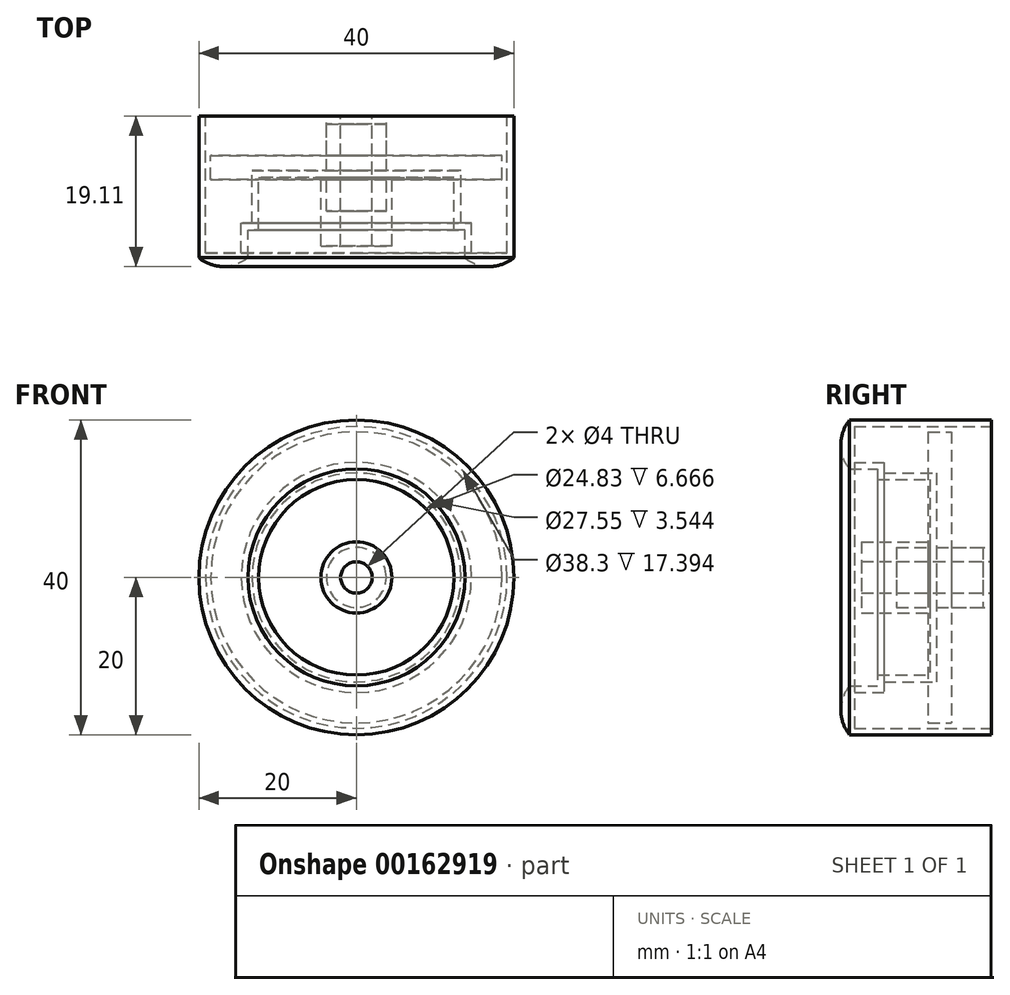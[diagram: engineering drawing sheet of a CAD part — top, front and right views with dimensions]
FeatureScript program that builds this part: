
annotation { "Feature Type Name" : "Feature", "Feature Type Description" : "" }
export const myFeature = defineFeature(function(context is Context, id is Id, definition is map)
    precondition{}
    {
        {
            var Q0;
            Q0=qCreatedBy(makeId("Top.planeOp"),FACE);
            var sketch = newSketch(context, id + "F0", { "sketchPlane" : qUnion([Q0])});
            skLineSegment(sketch, "E0", {"start": v(0, 17.4) * mm, "end": v(0, -20.43) * mm, "construction": true});
            skLineSegment(sketch, "E1", {"start": v(2, 6.54) * mm, "end": v(2, -9.96) * mm});
            skLineSegment(sketch, "E2", {"start": v(2, -9.96) * mm, "end": v(4.51, -9.96) * mm});
            skLineSegment(sketch, "E3", {"start": v(4.51, -9.96) * mm, "end": v(4.51, -1.25) * mm});
            skLineSegment(sketch, "E4", {"start": v(4.51, -1.25) * mm, "end": v(12.42, -1.25) * mm});
            skLineSegment(sketch, "E5", {"start": v(12.42, -1.25) * mm, "end": v(12.42, -7.92) * mm});
            skLineSegment(sketch, "E6", {"start": v(12.42, -7.92) * mm, "end": v(13.78, -7.92) * mm});
            skLineSegment(sketch, "E7", {"start": v(13.78, -7.92) * mm, "end": v(13.78, -11.46) * mm});
            skLineSegment(sketch, "E8", {"start": v(20, -11.46) * mm, "end": v(20, 6.54) * mm});
            skLineSegment(sketch, "E9.0", {"start": v(19.15, -10.86) * mm, "end": v(19.15, 6.54) * mm});
            skLineSegment(sketch, "E9.1", {"start": v(14.62, -10.86) * mm, "end": v(19.15, -10.86) * mm});
            skLineSegment(sketch, "E9.2", {"start": v(14.62, -7.07) * mm, "end": v(14.62, -10.86) * mm});
            skLineSegment(sketch, "E9.3", {"start": v(13.27, -7.07) * mm, "end": v(14.62, -7.07) * mm});
            skLineSegment(sketch, "E9.4", {"start": v(13.27, -0.4) * mm, "end": v(13.27, -7.07) * mm});
            skLineSegment(sketch, "E9.8", {"start": v(3.8, -0.4) * mm, "end": v(13.27, -0.4) * mm});
            skLineSegment(sketch, "E10", {"start": v(19.15, 6.54) * mm, "end": v(20, 6.54) * mm});
            skLineSegment(sketch, "E11", {"start": v(2, 6.54) * mm, "end": v(3.8, 6.54) * mm});
            skLineSegment(sketch, "E12", {"start": v(3.8, 6.54) * mm, "end": v(3.8, -0.4) * mm});
            skArc(sketch, "E13", {"start": v(13.78, -11.46) * mm, "mid": v(16.89, -12.57) * mm, "end": v(20, -11.46) * mm});
            skLineSegment(sketch, "E14", {"start": v(16.89, -10.86) * mm, "end": v(16.89, -7.65) * mm, "construction": true});
            skSolve(sketch);
        }
        {
            var Q0;
            Q0=makeQuery(id+"F0.imprint","IMPRINT",FACE,{"disambiguationData":[TD([[makeQuery(id+"F0.imprint","IMPRINT",EDGE,{"derivedFrom":sQuery(id+"F0.wireOp",EDGE,"E1")}),1.0]])]});
            var Q1;
            Q1=sQuery(id+"F0.wireOp",EDGE,"E0");
            revolve(context, id + "F1", {"entities" : qUnion([Q0]), "axis" : qUnion([Q1]), "revolveType" : RevolveType.FULL});
        }
        {
            var Q0;
            Q0=qCreatedBy(makeId("Top.planeOp"),FACE);
            var sketch = newSketch(context, id + "F2", { "sketchPlane" : qUnion([Q0])});
            skLineSegment(sketch, "E15.0", {"start": v(0, 17.4) * mm, "end": v(0, -20.43) * mm, "construction": true});
            skLineSegment(sketch, "E16.0", {"start": v(2, 5.5) * mm, "end": v(2, -5.5) * mm});
            skLineSegment(sketch, "E17", {"start": v(3.8, 5.5) * mm, "end": v(3.8, 1.5) * mm});
            skLineSegment(sketch, "E18", {"start": v(3.8, 1.5) * mm, "end": v(18.5, 1.5) * mm});
            skLineSegment(sketch, "E19", {"start": v(18.5, 1.5) * mm, "end": v(18.5, -1.5) * mm});
            skLineSegment(sketch, "E20", {"start": v(18.5, -1.5) * mm, "end": v(3.8, -1.5) * mm});
            skLineSegment(sketch, "E21", {"start": v(3.8, -1.5) * mm, "end": v(3.8, -5.5) * mm});
            skLineSegment(sketch, "E22", {"start": v(2, -5.5) * mm, "end": v(3.8, -5.5) * mm});
            skLineSegment(sketch, "E23", {"start": v(0, 0) * mm, "end": v(6.69, 0) * mm, "construction": true});
            skLineSegment(sketch, "E24", {"start": v(2, 5.5) * mm, "end": v(3.8, 5.5) * mm});
            skSolve(sketch);
        }
        {
            var Q0;
            Q0=makeQuery(id+"F2.imprint","IMPRINT",FACE,{"disambiguationData":[TD([[makeQuery(id+"F2.imprint","IMPRINT",EDGE,{"derivedFrom":sQuery(id+"F2.wireOp",EDGE,"E16.0")}),1.0]])]});
            var Q1;
            Q1=sQuery(id+"F2.wireOp",EDGE,"E15.0");
            revolve(context, id + "F3", {"entities" : qUnion([Q0]), "axis" : qUnion([Q1]), "revolveType" : RevolveType.FULL});
        }
    });
